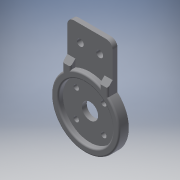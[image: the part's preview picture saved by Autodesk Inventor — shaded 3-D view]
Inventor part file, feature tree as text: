
AUTODESK INVENTOR PART (.ipt)
format: ipt  version: 2018 (Build 220112000, 112)  size: 220,160 bytes
history: native  units: in
note: dims shown in document units (in); Inventor stores cm internally (conversion verified against a paired STEP export)
features: extrude x4, sketch x4, projected_geometry x3, fillet x2, chamfer x1
ambient origin geometry x8: Origin, YZ Plane, XZ Plane, XY Plane, X Axis, Y Axis, Z Axis, Center Point
bodies: Solid1 (feature_tree)
feature tree (14):
  extrude  "Extrusion1"  Depth=1.7179in
  extrude  "Extrusion2"  Depth=1.1024in
  extrude  "Extrusion3"  Depth=0.7874in
  chamfer  "Chamfer1"  Distance=0.1969in
  fillet  "Fillet1"  Radius=0.1181in
  extrude  "Extrusion4"  Depth=0.3937in
  fillet  "Fillet2"  Radius=0.1654in
  sketch  "Sketch1"  dims[d0=1.6535in d1=1.7179in]
  sketch  "Sketch2"  dims[d2=0.1181in d3=0.0in d4=1.1024in]
  projected_geometry  "Projected Loop1"
  sketch  "Sketch3"  dims[d5=1.3189in d6=0.7874in]
  projected_geometry  "Projected Loop2"
  projected_geometry  "Projected Loop3"
  sketch  "Sketch4"  dims[d7=0.1969in d8=0.1969in d9=0.1181in d10=0.0in d11=0.3937in d12=0.1654in d13=0.4724in d14=0.3937in d15=0.1181in d16=0.0in d17=0.1181in d18=0.0787in d19=45.0deg d20=0.0394in d21=45.0deg d22=0.1299in d23=0.4724in d24=1.5748in d26=360.0deg d28=0.1181in d29=0.0in d30=0.1575in]
